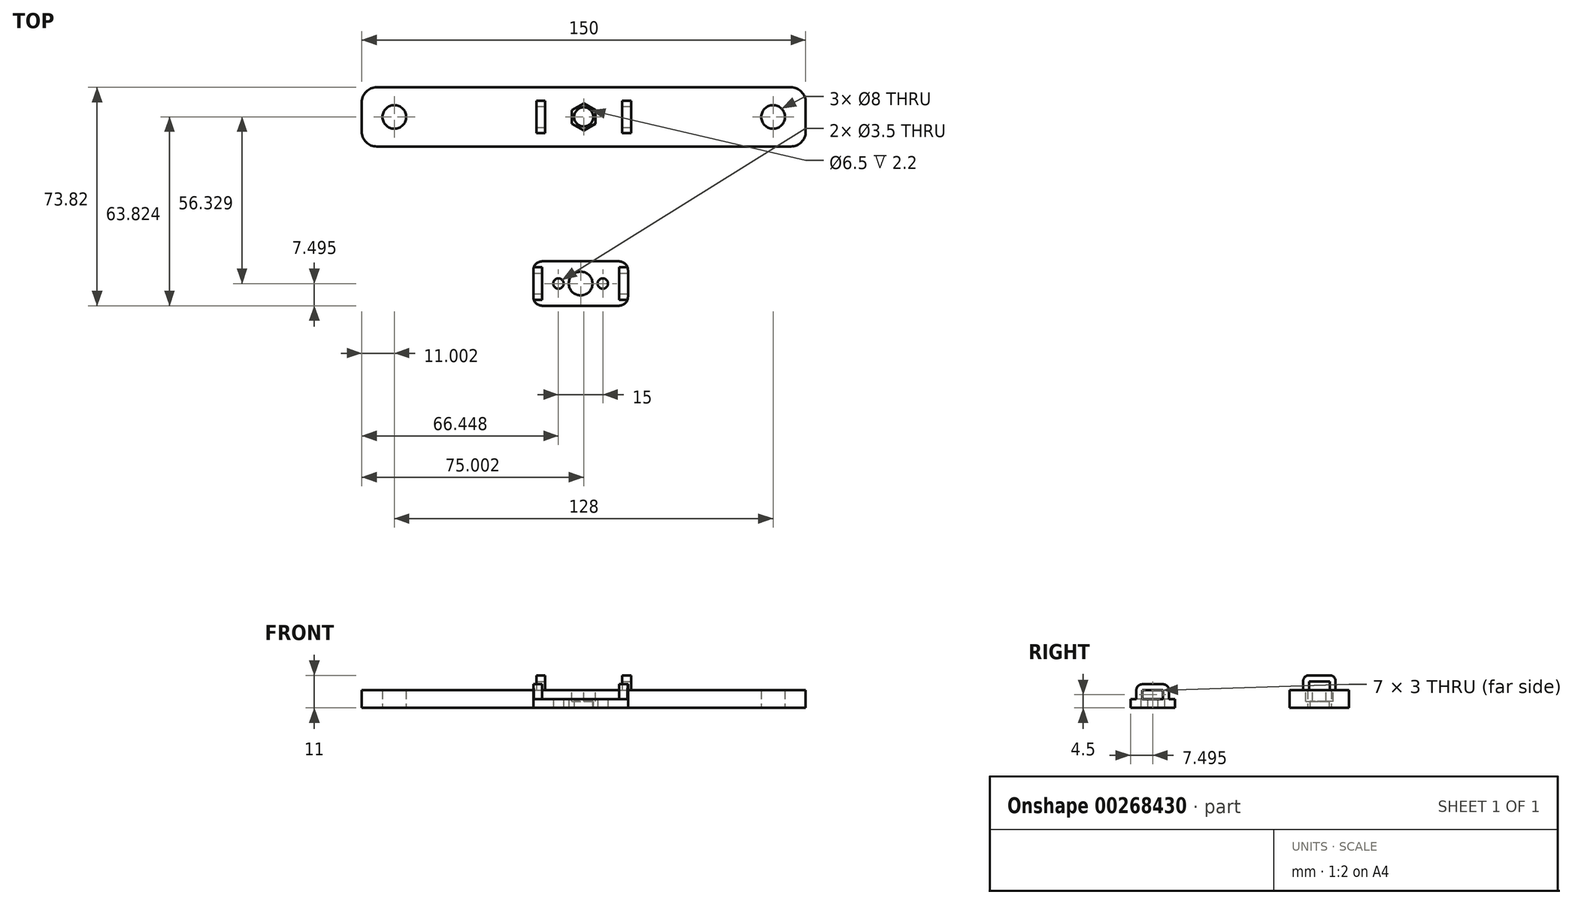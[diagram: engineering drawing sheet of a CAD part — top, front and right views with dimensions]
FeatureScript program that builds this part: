
annotation { "Feature Type Name" : "Feature", "Feature Type Description" : "" }
export const myFeature = defineFeature(function(context is Context, id is Id, definition is map)
    precondition{}
    {
        {
            var Q0;
            Q0=qCreatedBy(makeId("Top.planeOp"),FACE);
            var sketch = newSketch(context, id + "F0", { "sketchPlane" : qUnion([Q0])});
            skLineSegment(sketch, "E0.bottom", {"start": v(-104.35, 25.78) * mm, "end": v(35.65, 25.78) * mm});
            skLineSegment(sketch, "E0.top", {"start": v(-104.35, 5.78) * mm, "end": v(35.65, 5.78) * mm});
            skLineSegment(sketch, "E0.left", {"start": v(-109.35, 20.78) * mm, "end": v(-109.35, 10.78) * mm});
            skLineSegment(sketch, "E0.right", {"start": v(40.65, 20.78) * mm, "end": v(40.65, 10.78) * mm});
            skCircle(sketch, "E1", {"center": v(-98.35, 15.78) * mm, "radius": 4 * mm});
            skPoint(sketch, "E1.centerSnap0", {"position": v(-109.35, 15.78) * mm});
            skCircle(sketch, "E2", {"center": v(29.65, 15.78) * mm, "radius": 4 * mm});
            skCircle(sketch, "E3", {"center": v(-34.35, 15.78) * mm, "radius": 3.25 * mm});
            skPoint(sketch, "E3.centerSnap0", {"position": v(-34.35, 25.78) * mm});
            skPoint(sketch, "E4.visualSharp", {"position": v(-109.35, 25.78) * mm});
            skArc(sketch, "E4.filletArc", {"start": v(-104.35, 25.78) * mm, "mid": v(-107.88, 24.32) * mm, "end": v(-109.35, 20.78) * mm});
            skPoint(sketch, "E5.visualSharp", {"position": v(-109.35, 5.78) * mm});
            skArc(sketch, "E5.filletArc", {"start": v(-109.35, 10.78) * mm, "mid": v(-107.88, 7.25) * mm, "end": v(-104.35, 5.78) * mm});
            skPoint(sketch, "E6.visualSharp", {"position": v(40.65, 25.78) * mm});
            skArc(sketch, "E6.filletArc", {"start": v(40.65, 20.78) * mm, "mid": v(39.19, 24.32) * mm, "end": v(35.65, 25.78) * mm});
            skPoint(sketch, "E7.visualSharp", {"position": v(40.65, 5.78) * mm});
            skArc(sketch, "E7.filletArc", {"start": v(35.65, 5.78) * mm, "mid": v(39.19, 7.25) * mm, "end": v(40.65, 10.78) * mm});
            skSolve(sketch);
        }
        {
            var Q0;
            Q0=makeQuery(id+"F0.imprint","IMPRINT",FACE,{"disambiguationData":[TD([[makeQuery(id+"F0.imprint","IMPRINT",EDGE,{"derivedFrom":sQuery(id+"F0.wireOp",EDGE,"E0.bottom")}),-1.0]])]});
            extrude(context, id + "F1", {"entities" : qUnion([Q0]), "depth" : 6 * mm});
        }
        {
            var Q0;
            Q0=makeQuery(id+"F1.opExtrude","CAP_FACE",FACE,{"disambiguationData":[OSD([sQuery(id+"F0.wireOp",EDGE,"E0.bottom"),sQuery(id+"F0.wireOp",EDGE,"E0.top"),sQuery(id+"F0.wireOp",EDGE,"E0.left"),sQuery(id+"F0.wireOp",EDGE,"E0.right"),sQuery(id+"F0.wireOp",EDGE,"E1"),sQuery(id+"F0.wireOp",EDGE,"E2"),sQuery(id+"F0.wireOp",EDGE,"E3"),sQuery(id+"F0.wireOp",EDGE,"E4.filletArc"),sQuery(id+"F0.wireOp",EDGE,"E5.filletArc"),sQuery(id+"F0.wireOp",EDGE,"E6.filletArc"),sQuery(id+"F0.wireOp",EDGE,"E7.filletArc")])],"isStart":false});
            var sketch = newSketch(context, id + "F2", { "sketchPlane" : qUnion([Q0])});
            skCircle(sketch, "E8.cCircle", {"center": v(-34.35, 15.78) * mm, "radius": 4 * mm, "construction": true});
            skLineSegment(sketch, "E8.0", {"start": v(-30.35, 18.1) * mm, "end": v(-30.35, 13.47) * mm});
            skLineSegment(sketch, "E8.1", {"start": v(-30.35, 13.47) * mm, "end": v(-34.35, 11.17) * mm});
            skLineSegment(sketch, "E8.2", {"start": v(-34.35, 11.17) * mm, "end": v(-38.35, 13.47) * mm});
            skLineSegment(sketch, "E8.3", {"start": v(-38.35, 13.47) * mm, "end": v(-38.35, 18.1) * mm});
            skLineSegment(sketch, "E8.4", {"start": v(-38.35, 18.1) * mm, "end": v(-34.35, 20.4) * mm});
            skLineSegment(sketch, "E8.5", {"start": v(-34.35, 20.4) * mm, "end": v(-30.35, 18.1) * mm});
            skPoint(sketch, "E8.0.midPoint", {"position": v(-30.35, 15.78) * mm});
            skLineSegment(sketch, "E9.bottom", {"start": v(-50.35, 21.28) * mm, "end": v(-47.35, 21.28) * mm});
            skLineSegment(sketch, "E9.top", {"start": v(-50.35, 10.28) * mm, "end": v(-47.35, 10.28) * mm});
            skLineSegment(sketch, "E9.left", {"start": v(-50.35, 21.28) * mm, "end": v(-50.35, 10.28) * mm});
            skLineSegment(sketch, "E9.right", {"start": v(-47.35, 21.28) * mm, "end": v(-47.35, 10.28) * mm});
            skLineSegment(sketch, "E10.bottom", {"start": v(-21.35, 21.28) * mm, "end": v(-18.35, 21.28) * mm});
            skLineSegment(sketch, "E10.top", {"start": v(-21.35, 10.28) * mm, "end": v(-18.35, 10.28) * mm});
            skLineSegment(sketch, "E10.left", {"start": v(-21.35, 21.28) * mm, "end": v(-21.35, 10.28) * mm});
            skLineSegment(sketch, "E10.right", {"start": v(-18.35, 21.28) * mm, "end": v(-18.35, 10.28) * mm});
            skSolve(sketch);
        }
        {
            var Q0;
            Q0=makeQuery(id+"F2.imprint","IMPRINT",FACE,{"disambiguationData":[TD([[makeQuery(id+"F2.imprint","IMPRINT",EDGE,{"derivedFrom":sQuery(id+"F2.wireOp",EDGE,"E8.0")}),-1.0]])]});
            extrude(context, id + "F3", {"entities" : qUnion([Q0]), "operationType" : NewBodyOperationType.REMOVE, "oppositeDirection" : true, "depth" : 3.8 * mm});
        }
        {
            var Q0;
            Q0=makeQuery(id+"F2.imprint","IMPRINT",FACE,{"disambiguationData":[TD([[makeQuery(id+"F2.imprint","IMPRINT",EDGE,{"derivedFrom":sQuery(id+"F2.wireOp",EDGE,"E10.bottom")}),-1.0]])]});
            var Q1;
            Q1=makeQuery(id+"F2.imprint","IMPRINT",FACE,{"disambiguationData":[TD([[makeQuery(id+"F2.imprint","IMPRINT",EDGE,{"derivedFrom":sQuery(id+"F2.wireOp",EDGE,"E9.bottom")}),-1.0]])]});
            extrude(context, id + "F4", {"entities" : qUnion([Q0, Q1]), "operationType" : NewBodyOperationType.ADD, "depth" : 5 * mm});
        }
        {
            var Q0;
            Q0=makeQuery(id+"F4.opExtrude","CAP_EDGE",EDGE,{"disambiguationData":[OSD([sQuery(id+"F2.wireOp",EDGE,"E10.bottom")])],"isStart":false});
            var Q1;
            Q1=makeQuery(id+"F4.opExtrude","CAP_EDGE",EDGE,{"disambiguationData":[OSD([sQuery(id+"F2.wireOp",EDGE,"E10.top")])],"isStart":false});
            var Q2;
            Q2=makeQuery(id+"F4.opExtrude","CAP_EDGE",EDGE,{"disambiguationData":[OSD([sQuery(id+"F2.wireOp",EDGE,"E9.bottom")])],"isStart":false});
            var Q3;
            Q3=makeQuery(id+"F4.opExtrude","CAP_EDGE",EDGE,{"disambiguationData":[OSD([sQuery(id+"F2.wireOp",EDGE,"E9.top")])],"isStart":false});
            fillet(context, id + "F5", {"entities" : qUnion([Q0, Q1, Q2, Q3]), "radius" : 2 * mm, "tangentPropagation" : true, "allowEdgeOverflow" : false});
        }
        {
            var Q0;
            Q0=makeQuery(id+"F4.opExtrude","SWEPT_FACE",FACE,{"disambiguationData":[OSD([sQuery(id+"F2.wireOp",EDGE,"E10.right")])]});
            var sketch = newSketch(context, id + "F6", { "sketchPlane" : qUnion([Q0])});
            skLineSegment(sketch, "E11.bottom", {"start": v(12.28, 9) * mm, "end": v(19.28, 9) * mm});
            skLineSegment(sketch, "E11.top", {"start": v(12.28, 6) * mm, "end": v(19.28, 6) * mm});
            skLineSegment(sketch, "E11.left", {"start": v(12.28, 9) * mm, "end": v(12.28, 6) * mm});
            skLineSegment(sketch, "E11.right", {"start": v(19.28, 9) * mm, "end": v(19.28, 6) * mm});
            skSolve(sketch);
        }
        {
            var Q0;
            Q0=makeQuery(id+"F6.imprint","IMPRINT",FACE,{"disambiguationData":[TD([[makeQuery(id+"F6.imprint","IMPRINT",EDGE,{"derivedFrom":sQuery(id+"F6.wireOp",EDGE,"E11.bottom")}),-1.0]])]});
            extrude(context, id + "F7", {"entities" : qUnion([Q0]), "operationType" : NewBodyOperationType.REMOVE, "oppositeDirection" : true, "depth" : 35 * mm});
        }
        {
            var Q0;
            Q0=qCreatedBy(makeId("Top.planeOp"),FACE);
            var sketch = newSketch(context, id + "F8", { "sketchPlane" : qUnion([Q0])});
            skLineSegment(sketch, "E12.bottom", {"start": v(-48.4, -33.04) * mm, "end": v(-22.4, -33.04) * mm});
            skLineSegment(sketch, "E12.top", {"start": v(-48.4, -48.04) * mm, "end": v(-22.4, -48.04) * mm});
            skLineSegment(sketch, "E12.left", {"start": v(-51.4, -36.04) * mm, "end": v(-51.4, -45.04) * mm});
            skLineSegment(sketch, "E12.right", {"start": v(-19.4, -36.04) * mm, "end": v(-19.4, -45.04) * mm});
            skCircle(sketch, "E13", {"center": v(-35.4, -40.54) * mm, "radius": 4 * mm});
            skPoint(sketch, "E13.centerSnap0", {"position": v(-51.4, -40.54) * mm});
            skPoint(sketch, "E13.centerSnap1", {"position": v(-35.4, -33.04) * mm});
            skCircle(sketch, "E14", {"center": v(-42.9, -40.54) * mm, "radius": 1.75 * mm});
            skCircle(sketch, "E15", {"center": v(-27.9, -40.54) * mm, "radius": 1.75 * mm});
            skPoint(sketch, "E16.visualSharp", {"position": v(-51.4, -33.04) * mm});
            skArc(sketch, "E16.filletArc", {"start": v(-48.4, -33.04) * mm, "mid": v(-50.52, -33.92) * mm, "end": v(-51.4, -36.04) * mm});
            skPoint(sketch, "E17.visualSharp", {"position": v(-51.4, -48.04) * mm});
            skArc(sketch, "E17.filletArc", {"start": v(-51.4, -45.04) * mm, "mid": v(-50.52, -47.17) * mm, "end": v(-48.4, -48.04) * mm});
            skPoint(sketch, "E18.visualSharp", {"position": v(-19.4, -48.04) * mm});
            skArc(sketch, "E18.filletArc", {"start": v(-22.4, -48.04) * mm, "mid": v(-20.28, -47.17) * mm, "end": v(-19.4, -45.04) * mm});
            skPoint(sketch, "E19.visualSharp", {"position": v(-19.4, -33.04) * mm});
            skArc(sketch, "E19.filletArc", {"start": v(-19.4, -36.04) * mm, "mid": v(-20.28, -33.92) * mm, "end": v(-22.4, -33.04) * mm});
            skSolve(sketch);
        }
        {
            var Q0;
            Q0=makeQuery(id+"F8.imprint","IMPRINT",FACE,{"disambiguationData":[TD([[makeQuery(id+"F8.imprint","IMPRINT",EDGE,{"derivedFrom":sQuery(id+"F8.wireOp",EDGE,"E12.bottom")}),-1.0]])]});
            extrude(context, id + "F9", {"entities" : qUnion([Q0]), "depth" : 3 * mm});
        }
        {
            var Q0;
            Q0=makeQuery(id+"F9.opExtrude","CAP_FACE",FACE,{"disambiguationData":[OSD([sQuery(id+"F8.wireOp",EDGE,"E12.bottom"),sQuery(id+"F8.wireOp",EDGE,"E12.top"),sQuery(id+"F8.wireOp",EDGE,"E12.left"),sQuery(id+"F8.wireOp",EDGE,"E12.right"),sQuery(id+"F8.wireOp",EDGE,"E13"),sQuery(id+"F8.wireOp",EDGE,"E14"),sQuery(id+"F8.wireOp",EDGE,"E15"),sQuery(id+"F8.wireOp",EDGE,"E16.filletArc"),sQuery(id+"F8.wireOp",EDGE,"E17.filletArc"),sQuery(id+"F8.wireOp",EDGE,"E18.filletArc"),sQuery(id+"F8.wireOp",EDGE,"E19.filletArc")])],"isStart":false});
            var sketch = newSketch(context, id + "F10", { "sketchPlane" : qUnion([Q0])});
            skLineSegment(sketch, "E20.bottom", {"start": v(-51.4, -35.04) * mm, "end": v(-48.4, -35.04) * mm});
            skLineSegment(sketch, "E20.top", {"start": v(-51.4, -46.04) * mm, "end": v(-48.4, -46.04) * mm});
            skLineSegment(sketch, "E20.left", {"start": v(-51.4, -35.04) * mm, "end": v(-51.4, -46.04) * mm});
            skLineSegment(sketch, "E20.right", {"start": v(-48.4, -35.04) * mm, "end": v(-48.4, -46.04) * mm});
            skLineSegment(sketch, "E21.bottom", {"start": v(-22.4, -35.04) * mm, "end": v(-19.4, -35.04) * mm});
            skLineSegment(sketch, "E21.top", {"start": v(-22.4, -46.04) * mm, "end": v(-19.4, -46.04) * mm});
            skLineSegment(sketch, "E21.left", {"start": v(-22.4, -35.04) * mm, "end": v(-22.4, -46.04) * mm});
            skLineSegment(sketch, "E21.right", {"start": v(-19.4, -35.04) * mm, "end": v(-19.4, -46.04) * mm});
            skSolve(sketch);
        }
        {
            var Q0;
            {var subQ5=sQuery(id+"F10.wireOp",EDGE,"E21.left");Q0=makeQuery(id+"F10.imprint","IMPRINT",FACE,{"disambiguationData":[TD([[makeQuery(id+"F10.imprint","IMPRINT",EDGE,{"derivedFrom":subQ5}),1.0]])]});}
            var Q1;
            {var subQ0=sQuery(id+"F10.wireOp",EDGE,"E20.right");Q1=makeQuery(id+"F10.imprint","IMPRINT",FACE,{"disambiguationData":[TD([[makeQuery(id+"F10.imprint","IMPRINT",EDGE,{"derivedFrom":subQ0}),-1.0]])]});}
            extrude(context, id + "F11", {"entities" : qUnion([Q0, Q1]), "operationType" : NewBodyOperationType.ADD, "depth" : 5 * mm});
        }
        {
            var Q0;
            Q0=makeQuery(id+"F11.opExtrude","SWEPT_FACE",FACE,{"disambiguationData":[OSD([sQuery(id+"F10.wireOp",EDGE,"E21.right")])]});
            var sketch = newSketch(context, id + "F12", { "sketchPlane" : qUnion([Q0])});
            skLineSegment(sketch, "E22.bottom", {"start": v(-44.04, 6) * mm, "end": v(-37.04, 6) * mm});
            skLineSegment(sketch, "E22.top", {"start": v(-44.04, 3) * mm, "end": v(-37.04, 3) * mm});
            skLineSegment(sketch, "E22.left", {"start": v(-44.04, 6) * mm, "end": v(-44.04, 3) * mm});
            skLineSegment(sketch, "E22.right", {"start": v(-37.04, 6) * mm, "end": v(-37.04, 3) * mm});
            skSolve(sketch);
        }
        {
            var Q0;
            Q0=makeQuery(id+"F12.imprint","IMPRINT",FACE,{"disambiguationData":[TD([[makeQuery(id+"F12.imprint","IMPRINT",EDGE,{"derivedFrom":sQuery(id+"F12.wireOp",EDGE,"E22.bottom")}),-1.0]])]});
            extrude(context, id + "F13", {"entities" : qUnion([Q0]), "operationType" : NewBodyOperationType.REMOVE, "oppositeDirection" : true, "depth" : 35 * mm});
        }
        {
            var Q0;
            Q0=makeQuery(id+"F11.opExtrude","CAP_EDGE",EDGE,{"disambiguationData":[OSD([sQuery(id+"F10.wireOp",EDGE,"E21.top")])],"isStart":false});
            var Q1;
            Q1=makeQuery(id+"F11.opExtrude","CAP_EDGE",EDGE,{"disambiguationData":[OSD([sQuery(id+"F10.wireOp",EDGE,"E20.top")])],"isStart":false});
            var Q2;
            Q2=makeQuery(id+"F11.opExtrude","CAP_EDGE",EDGE,{"disambiguationData":[OSD([sQuery(id+"F10.wireOp",EDGE,"E20.bottom")])],"isStart":false});
            var Q3;
            Q3=makeQuery(id+"F11.opExtrude","CAP_EDGE",EDGE,{"disambiguationData":[OSD([sQuery(id+"F10.wireOp",EDGE,"E21.bottom")])],"isStart":false});
            fillet(context, id + "F14", {"entities" : qUnion([Q0, Q1, Q2, Q3]), "radius" : 2 * mm, "tangentPropagation" : true, "allowEdgeOverflow" : false});
        }
    });
